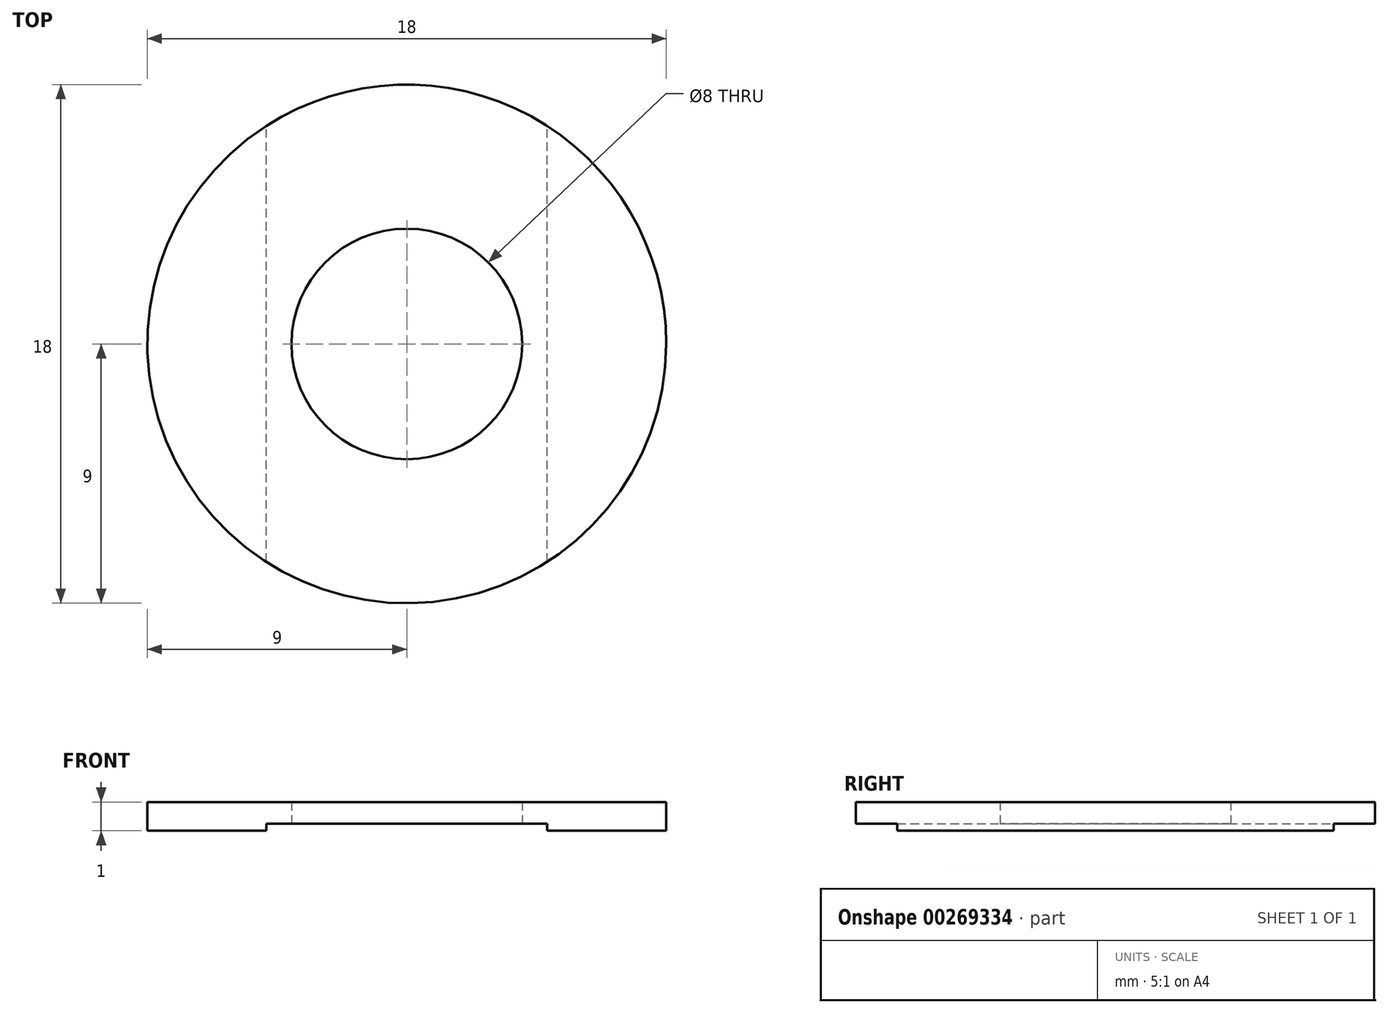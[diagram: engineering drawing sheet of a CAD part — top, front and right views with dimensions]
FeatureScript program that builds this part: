
annotation { "Feature Type Name" : "Feature", "Feature Type Description" : "" }
export const myFeature = defineFeature(function(context is Context, id is Id, definition is map)
    precondition{}
    {
        {
            var Q0;
            Q0=qCreatedBy(makeId("Top.planeOp"),FACE);
            var sketch = newSketch(context, id + "F0", { "sketchPlane" : qUnion([Q0])});
            skCircle(sketch, "E0", {"center": v(0, 0) * mm, "radius": 4 * mm});
            skCircle(sketch, "E1", {"center": v(0, 0) * mm, "radius": 9 * mm});
            skSolve(sketch);
        }
        {
            var Q0;
            Q0=makeQuery(id+"F0.imprint","IMPRINT",FACE,{"disambiguationData":[TD([[makeQuery(id+"F0.imprint","IMPRINT",EDGE,{"derivedFrom":sQuery(id+"F0.wireOp",EDGE,"E0")}),-1.0]])]});
            extrude(context, id + "F1", {"entities" : qUnion([Q0]), "depth" : 1 * mm});
        }
        {
            var Q0;
            Q0=makeQuery(id+"F1.opExtrude","CAP_FACE",FACE,{"disambiguationData":[OSD([sQuery(id+"F0.wireOp",EDGE,"E0"),sQuery(id+"F0.wireOp",EDGE,"E1")])],"isStart":true});
            var sketch = newSketch(context, id + "F2", { "sketchPlane" : qUnion([Q0])});
            skLineSegment(sketch, "E2.bottom", {"start": v(4.88, 9) * mm, "end": v(-4.88, 9) * mm});
            skLineSegment(sketch, "E2.top", {"start": v(4.88, -9) * mm, "end": v(-4.88, -9) * mm});
            skLineSegment(sketch, "E2.left", {"start": v(4.88, 9) * mm, "end": v(4.88, -9) * mm});
            skLineSegment(sketch, "E2.right", {"start": v(-4.88, 9) * mm, "end": v(-4.88, -9) * mm});
            skPoint(sketch, "E2.middle", {"position": v(0, 0) * mm});
            skSolve(sketch);
        }
        {
            var Q0;
            Q0=makeQuery(id+"F2.imprint","IMPRINT",FACE,{"disambiguationData":[TD([[makeQuery(id+"F2.imprint","IMPRINT",EDGE,{"derivedFrom":makeQuery(id+"F1.opExtrude","CAP_EDGE",EDGE,{"disambiguationData":[OSD([sQuery(id+"F0.wireOp",EDGE,"E0")])],"isStart":true})}),1.0]])]});
            extrude(context, id + "F3", {"entities" : qUnion([Q0]), "operationType" : NewBodyOperationType.REMOVE, "oppositeDirection" : true, "depth" : .25 * mm});
        }
    });
